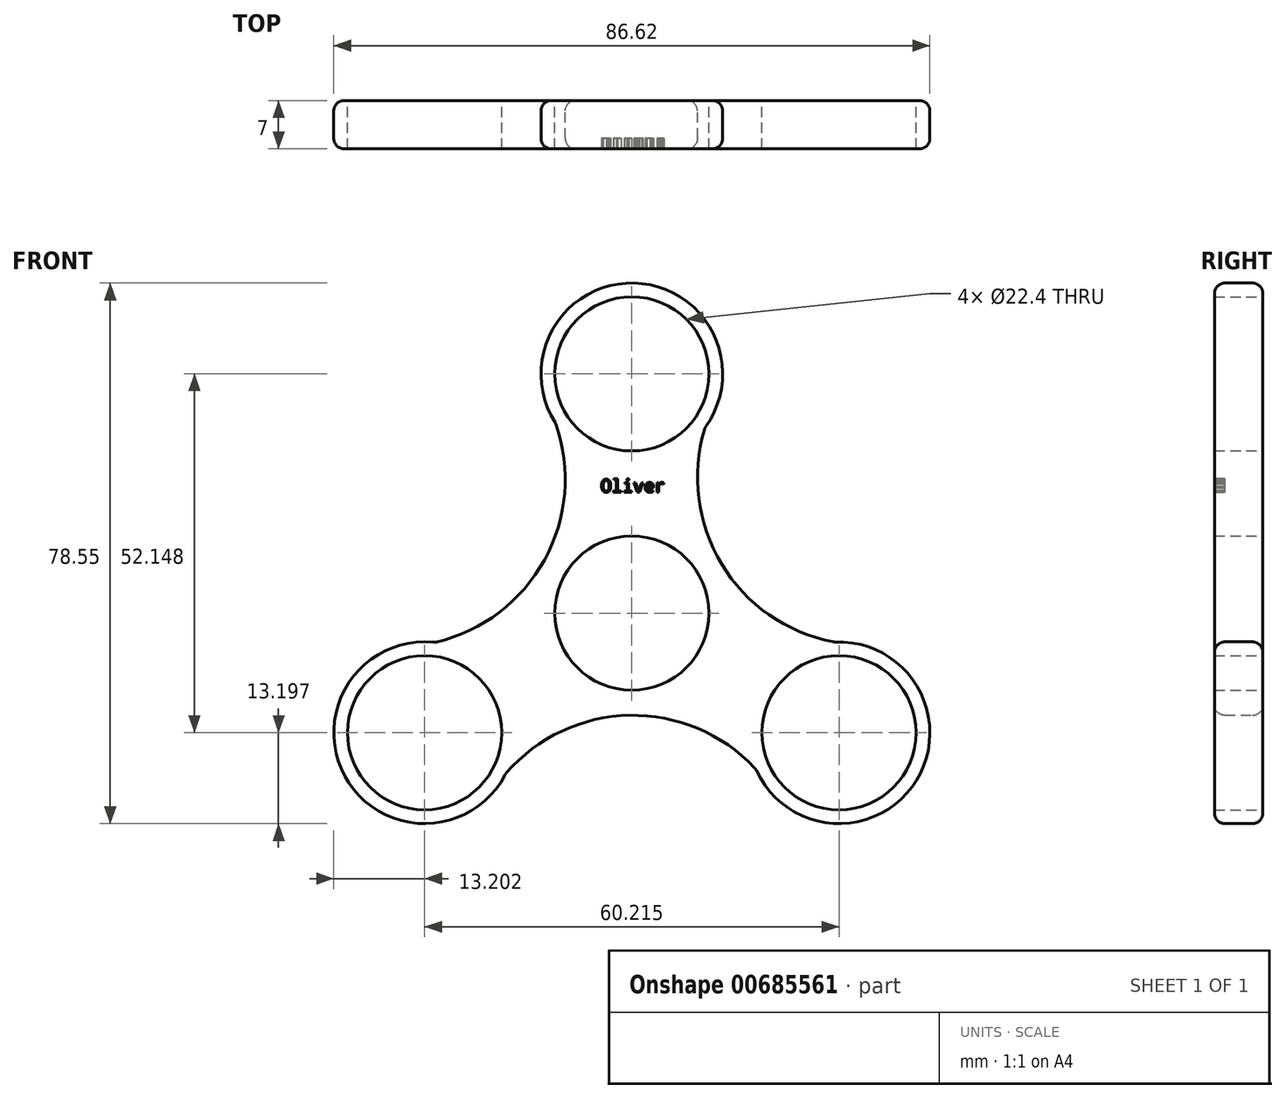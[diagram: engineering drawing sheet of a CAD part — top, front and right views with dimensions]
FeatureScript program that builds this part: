
annotation { "Feature Type Name" : "Feature", "Feature Type Description" : "" }
export const myFeature = defineFeature(function(context is Context, id is Id, definition is map)
    precondition{}
    {
        {
            var Q0;
            Q0=qCreatedBy(makeId("Front.planeOp"),FACE);
            var sketch = newSketch(context, id + "F0", { "sketchPlane" : qUnion([Q0])});
            skCircle(sketch, "E0", {"center": v(0, 0) * mm, "radius": 11.2 * mm});
            skCircle(sketch, "E1", {"center": v(0, 34.77) * mm, "radius": 11.2 * mm});
            skArc(sketch, "E2", {"start": v(10.63, 26.94) * mm, "mid": v(0.38, 47.96) * mm, "end": v(-11.06, 27.56) * mm});
            skCircle(sketch, "E3.1.0", {"center": v(-30.1, -17.38) * mm, "radius": 11.2 * mm});
            skArc(sketch, "E3.1.1", {"start": v(-28.65, -4.26) * mm, "mid": v(-41.72, -23.65) * mm, "end": v(-18.34, -23.36) * mm});
            skCircle(sketch, "E3.2.0", {"center": v(30.1, -17.38) * mm, "radius": 11.2 * mm});
            skArc(sketch, "E3.2.1", {"start": v(18.02, -22.68) * mm, "mid": v(41.35, -24.3) * mm, "end": v(29.4, -4.2) * mm});
            skArc(sketch, "E4", {"start": v(10.63, 26.94) * mm, "mid": v(13.02, 7.15) * mm, "end": v(29.4, -4.2) * mm});
            skArc(sketch, "E5.1.0", {"start": v(-28.65, -4.26) * mm, "mid": v(-12.7, 7.7) * mm, "end": v(-11.06, 27.56) * mm});
            skArc(sketch, "E5.2.0", {"start": v(18.02, -22.68) * mm, "mid": v(-0.31, -14.85) * mm, "end": v(-18.34, -23.36) * mm});
            skSolve(sketch);
        }
        {
            var Q0;
            Q0 = qSketchRegion(id + "F0", true);
            extrude(context, id + "F1", {"entities" : qUnion([Q0]), "depth" : 7 * mm, "offsetDistance" : 25 * mm});
        }
        {
            var Q0;
            Q0=makeQuery(id+"F1.opExtrude","SWEPT_FACE",FACE,{"disambiguationData":[OSD([sQuery(id+"F0.wireOp",EDGE,"E4")])]});
            var Q1;
            Q1=makeQuery(id+"F1.opExtrude","CAP_EDGE",EDGE,{"disambiguationData":[OSD([sQuery(id+"F0.wireOp",EDGE,"E3.2.1")])],"isStart":false});
            var Q2;
            Q2=makeQuery(id+"F1.opExtrude","CAP_EDGE",EDGE,{"disambiguationData":[OSD([sQuery(id+"F0.wireOp",EDGE,"E3.2.1")])],"isStart":true});
            var Q3;
            Q3=makeQuery(id+"F1.opExtrude","SWEPT_FACE",FACE,{"disambiguationData":[OSD([sQuery(id+"F0.wireOp",EDGE,"E5.2.0")])]});
            var Q4;
            Q4=makeQuery(id+"F1.opExtrude","CAP_EDGE",EDGE,{"disambiguationData":[OSD([sQuery(id+"F0.wireOp",EDGE,"E3.1.1")])],"isStart":false});
            var Q5;
            Q5=makeQuery(id+"F1.opExtrude","CAP_EDGE",EDGE,{"disambiguationData":[OSD([sQuery(id+"F0.wireOp",EDGE,"E3.1.1")])],"isStart":true});
            var Q6;
            Q6=makeQuery(id+"F1.opExtrude","SWEPT_FACE",FACE,{"disambiguationData":[OSD([sQuery(id+"F0.wireOp",EDGE,"E5.1.0")])]});
            var Q7;
            Q7=makeQuery(id+"F1.opExtrude","SWEPT_FACE",FACE,{"disambiguationData":[OSD([sQuery(id+"F0.wireOp",EDGE,"E2")])]});
            var Q8;
            Q8=makeQuery(id+"F1.opExtrude","SWEPT_FACE",FACE,{"disambiguationData":[OSD([sQuery(id+"F0.wireOp",EDGE,"E3.2.1")])]});
            fillet(context, id + "F2", {"entities" : qUnion([Q0, Q1, Q2, Q3, Q4, Q5, Q6, Q7, Q8]), "radius" : 1.5 * mm, "tangentPropagation" : true, "allowEdgeOverflow" : false});
        }
        {
            var Q0;
            Q0=makeQuery(id+"F1.opExtrude","CAP_FACE",FACE,{"disambiguationData":[OSD([sQuery(id+"F0.wireOp",EDGE,"E0"),sQuery(id+"F0.wireOp",EDGE,"E1"),sQuery(id+"F0.wireOp",EDGE,"E2"),sQuery(id+"F0.wireOp",EDGE,"E3.1.0"),sQuery(id+"F0.wireOp",EDGE,"E3.1.1"),sQuery(id+"F0.wireOp",EDGE,"E3.2.0"),sQuery(id+"F0.wireOp",EDGE,"E3.2.1"),sQuery(id+"F0.wireOp",EDGE,"E4"),sQuery(id+"F0.wireOp",EDGE,"E5.1.0"),sQuery(id+"F0.wireOp",EDGE,"E5.2.0")])],"isStart":false});
            var sketch = newSketch(context, id + "F3", { "sketchPlane" : qUnion([Q0])});
            skText(sketch, "E6", { "text": "Oliver", "fontName": "DroidSansMono.ttf"});
            const initialGuessF3  = {"E6": [-0.00451, 0.01757, 1, 0, 0.00188]};
            skSetInitialGuess(sketch, initialGuessF3);
            skSolve(sketch);
        }
        {
            var Q0;
            Q0 = qSketchRegion(id + "F3", true);
            extrude(context, id + "F4", {"entities" : qUnion([Q0]), "operationType" : NewBodyOperationType.REMOVE, "oppositeDirection" : true, "depth" : 1.5 * mm, "offsetDistance" : 25 * mm});
        }
    });
